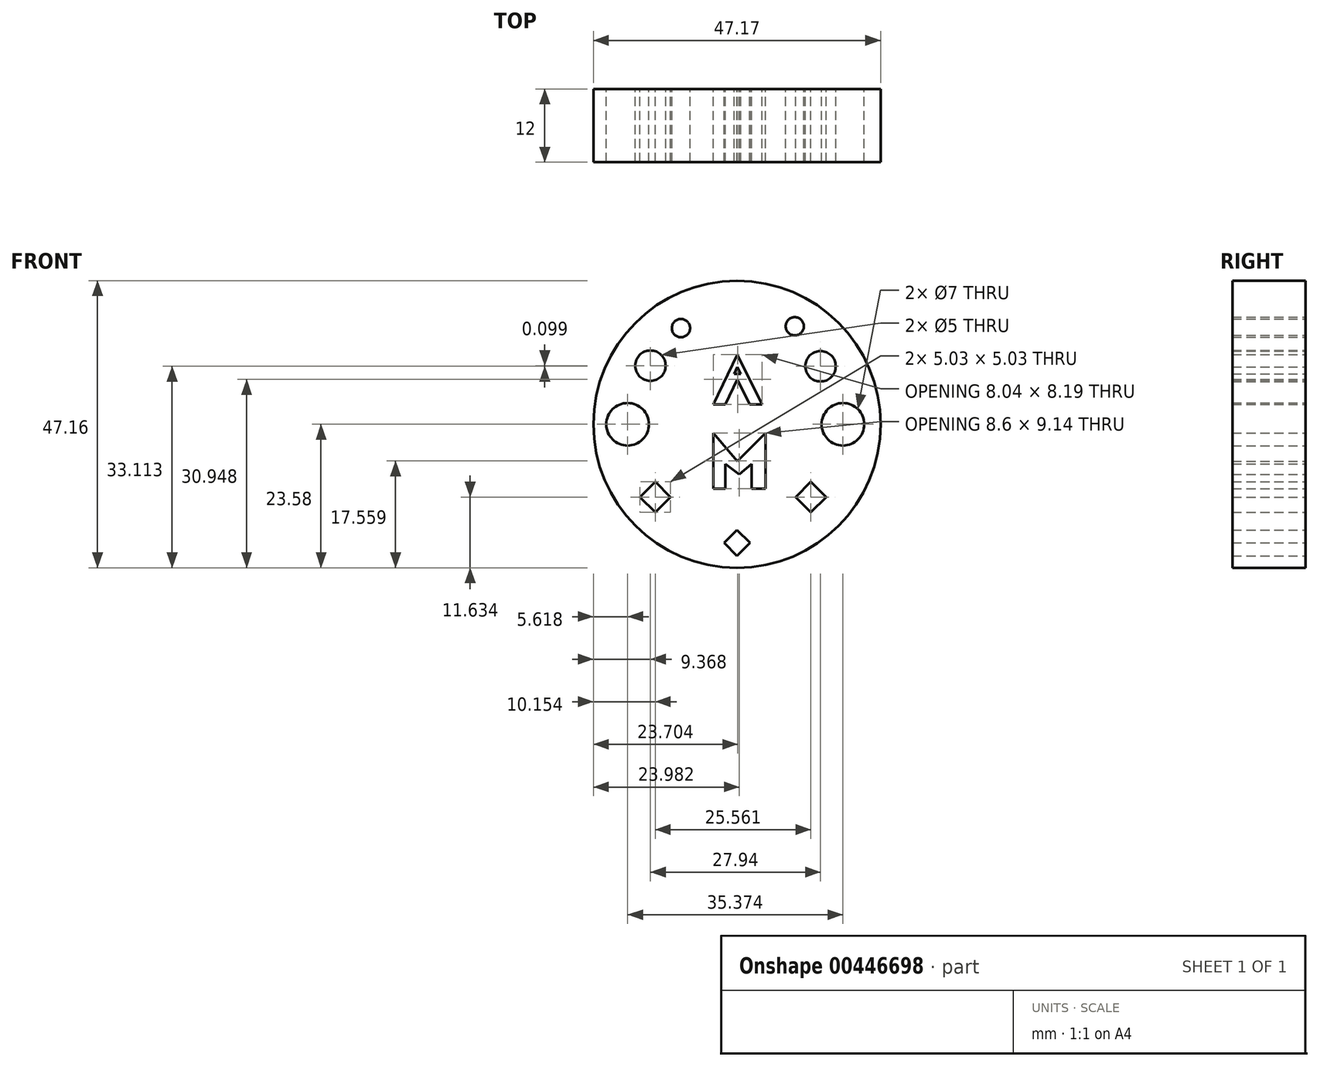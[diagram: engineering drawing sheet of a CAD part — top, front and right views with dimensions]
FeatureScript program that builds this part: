
annotation { "Feature Type Name" : "Feature", "Feature Type Description" : "" }
export const myFeature = defineFeature(function(context is Context, id is Id, definition is map)
    precondition{}
    {
        {
            var Q0;
            Q0=qCreatedBy(makeId("Front.planeOp"),FACE);
            var sketch = newSketch(context, id + "F0", { "sketchPlane" : qUnion([Q0])});
            skLineSegment(sketch, "E0", {"start": v(0.15, 14.18) * mm, "end": v(-3.83, 6) * mm});
            skLineSegment(sketch, "E1", {"start": v(-3.83, 6) * mm, "end": v(0.15, 14.18) * mm});
            skLineSegment(sketch, "E2", {"start": v(4.22, 6) * mm, "end": v(0.15, 14.18) * mm});
            skLineSegment(sketch, "E3", {"start": v(-3.83, 6) * mm, "end": v(-1.84, 6) * mm});
            skPoint(sketch, "E3.endSnap0", {"position": v(-1.84, 10.09) * mm});
            skLineSegment(sketch, "E4", {"start": v(4.22, 6) * mm, "end": v(2.18, 6) * mm});
            skPoint(sketch, "E4.endSnap0", {"position": v(2.18, 10.09) * mm});
            skLineSegment(sketch, "E5", {"start": v(2.18, 6) * mm, "end": v(0.15, 10.09) * mm});
            skLineSegment(sketch, "E6", {"start": v(0.15, 10.09) * mm, "end": v(-1.84, 6) * mm});
            skLineSegment(sketch, "E7", {"start": v(0.15, 12.15) * mm, "end": v(-0.4, 11) * mm});
            skLineSegment(sketch, "E8", {"start": v(-0.4, 11) * mm, "end": v(0.7, 11) * mm});
            skLineSegment(sketch, "E9", {"start": v(0.7, 11) * mm, "end": v(0.15, 12.15) * mm});
            skLineSegment(sketch, "E10", {"start": v(-3.83, 1.27) * mm, "end": v(-3.83, -7.87) * mm});
            skLineSegment(sketch, "E11", {"start": v(-3.83, 1.27) * mm, "end": v(0.15, -3.35) * mm});
            skLineSegment(sketch, "E12", {"start": v(0.15, -3.35) * mm, "end": v(4.77, 1.27) * mm});
            skLineSegment(sketch, "E13", {"start": v(4.77, 1.27) * mm, "end": v(4.77, -7.87) * mm});
            skLineSegment(sketch, "E14", {"start": v(-3.83, -7.87) * mm, "end": v(-1.84, -7.87) * mm});
            skPoint(sketch, "E14.endSnap0", {"position": v(-1.84, -1.04) * mm});
            skLineSegment(sketch, "E15", {"start": v(4.77, -7.87) * mm, "end": v(2.46, -7.87) * mm});
            skPoint(sketch, "E15.endSnap0", {"position": v(2.46, -1.04) * mm});
            skLineSegment(sketch, "E16", {"start": v(2.46, -7.87) * mm, "end": v(2.46, -3.77) * mm});
            skLineSegment(sketch, "E17", {"start": v(2.46, -3.77) * mm, "end": v(0.47, -5.48) * mm});
            skLineSegment(sketch, "E18", {"start": v(-1.84, -7.87) * mm, "end": v(-1.84, -3.77) * mm});
            skLineSegment(sketch, "E19", {"start": v(-1.84, -3.77) * mm, "end": v(0.47, -5.48) * mm});
            skCircle(sketch, "E20", {"center": v(0.08, 2.72) * mm, "radius": 23.58 * mm});
            skCircle(sketch, "E21", {"center": v(17.48, 2.72) * mm, "radius": 3.5 * mm});
            skCircle(sketch, "E22", {"center": v(-17.9, 2.72) * mm, "radius": 3.5 * mm});
            skCircle(sketch, "E23", {"center": v(-14.14, 12.35) * mm, "radius": 2.5 * mm});
            skCircle(sketch, "E24", {"center": v(-9.13, 18.51) * mm, "radius": 1.5 * mm});
            skCircle(sketch, "E25", {"center": v(9.57, 18.82) * mm, "radius": 1.5 * mm});
            skCircle(sketch, "E26", {"center": v(13.8, 12.25) * mm, "radius": 2.5 * mm});
            skLineSegment(sketch, "E27", {"start": v(0.08, -14.63) * mm, "end": v(-2.05, -16.75) * mm});
            skLineSegment(sketch, "E28", {"start": v(-2.05, -16.75) * mm, "end": v(0.08, -18.88) * mm});
            skLineSegment(sketch, "E29", {"start": v(0.08, -18.88) * mm, "end": v(2.2, -16.75) * mm});
            skLineSegment(sketch, "E30", {"start": v(2.2, -16.75) * mm, "end": v(0.08, -14.63) * mm});
            skLineSegment(sketch, "E31", {"start": v(-13.36, -6.71) * mm, "end": v(-15.87, -9.23) * mm});
            skLineSegment(sketch, "E32", {"start": v(-15.87, -9.23) * mm, "end": v(-13.36, -11.74) * mm});
            skLineSegment(sketch, "E33", {"start": v(-13.36, -11.74) * mm, "end": v(-10.84, -9.23) * mm});
            skLineSegment(sketch, "E34", {"start": v(-10.84, -9.23) * mm, "end": v(-13.36, -6.71) * mm});
            skLineSegment(sketch, "E35", {"start": v(9.7, -9.23) * mm, "end": v(12.2, -6.71) * mm});
            skLineSegment(sketch, "E36", {"start": v(12.2, -6.71) * mm, "end": v(14.72, -9.23) * mm});
            skLineSegment(sketch, "E37", {"start": v(14.72, -9.23) * mm, "end": v(12.2, -11.74) * mm});
            skLineSegment(sketch, "E38", {"start": v(12.2, -11.74) * mm, "end": v(9.7, -9.23) * mm});
            skSolve(sketch);
        }
        {
            var Q0;
            Q0 = qSketchRegion(id + "F0", true);
            var Q1;
            Q1=makeQuery(id+"F0.imprint","IMPRINT",FACE,{"disambiguationData":[TD([[makeQuery(id+"F0.imprint","IMPRINT",EDGE,{"derivedFrom":sQuery(id+"F0.wireOp",EDGE,"E7")}),1.0]])]});
            extrude(context, id + "F1", {"entities" : qUnion([Q0, Q1]), "depth" : 12 * mm});
        }
    });
